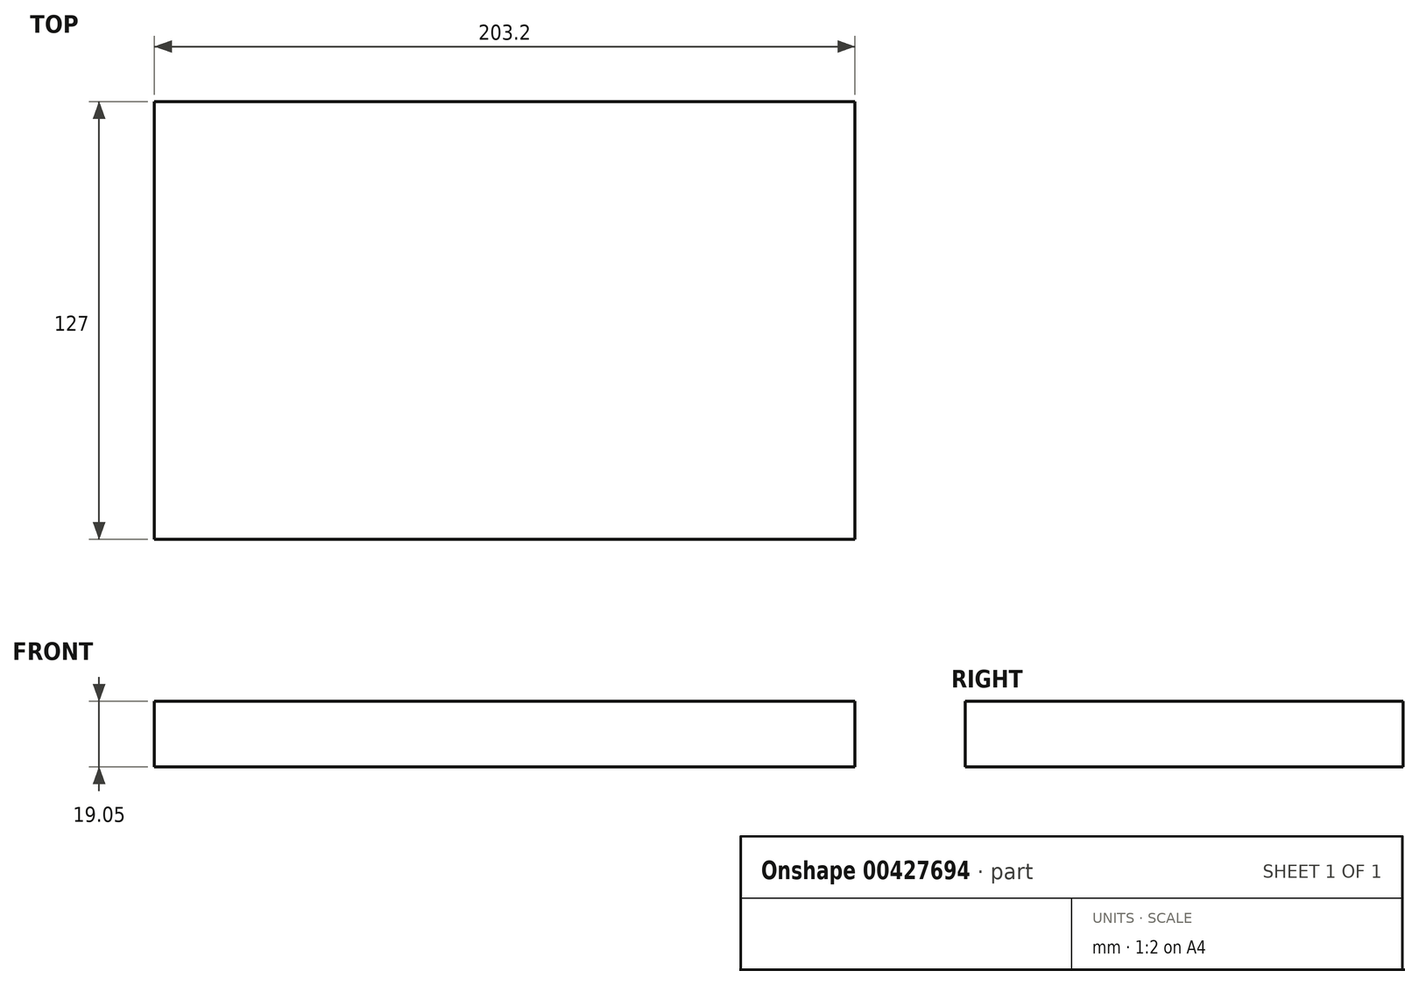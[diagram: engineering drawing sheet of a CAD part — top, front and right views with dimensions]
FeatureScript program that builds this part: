
annotation { "Feature Type Name" : "Feature", "Feature Type Description" : "" }
export const myFeature = defineFeature(function(context is Context, id is Id, definition is map)
    precondition{}
    {
        {
            var Q0;
            Q0=qCreatedBy(makeId("Top.planeOp"),FACE);
            var sketch = newSketch(context, id + "F0", { "sketchPlane" : qUnion([Q0])});
            skLineSegment(sketch, "E0.bottom", {"start": v(101.6, 63.5) * mm, "end": v(-101.6, 63.5) * mm});
            skLineSegment(sketch, "E0.top", {"start": v(101.6, -63.5) * mm, "end": v(-101.6, -63.5) * mm});
            skLineSegment(sketch, "E0.left", {"start": v(101.6, 63.5) * mm, "end": v(101.6, -63.5) * mm});
            skLineSegment(sketch, "E0.right", {"start": v(-101.6, 63.5) * mm, "end": v(-101.6, -63.5) * mm});
            skPoint(sketch, "E0.middle", {"position": v(0, 0) * mm});
            skSolve(sketch);
        }
        {
            var Q0;
            Q0 = qSketchRegion(id + "F0", true);
            extrude(context, id + "F1", {"entities" : qUnion([Q0]), "depth" : 19.05 * mm});
        }
    });
